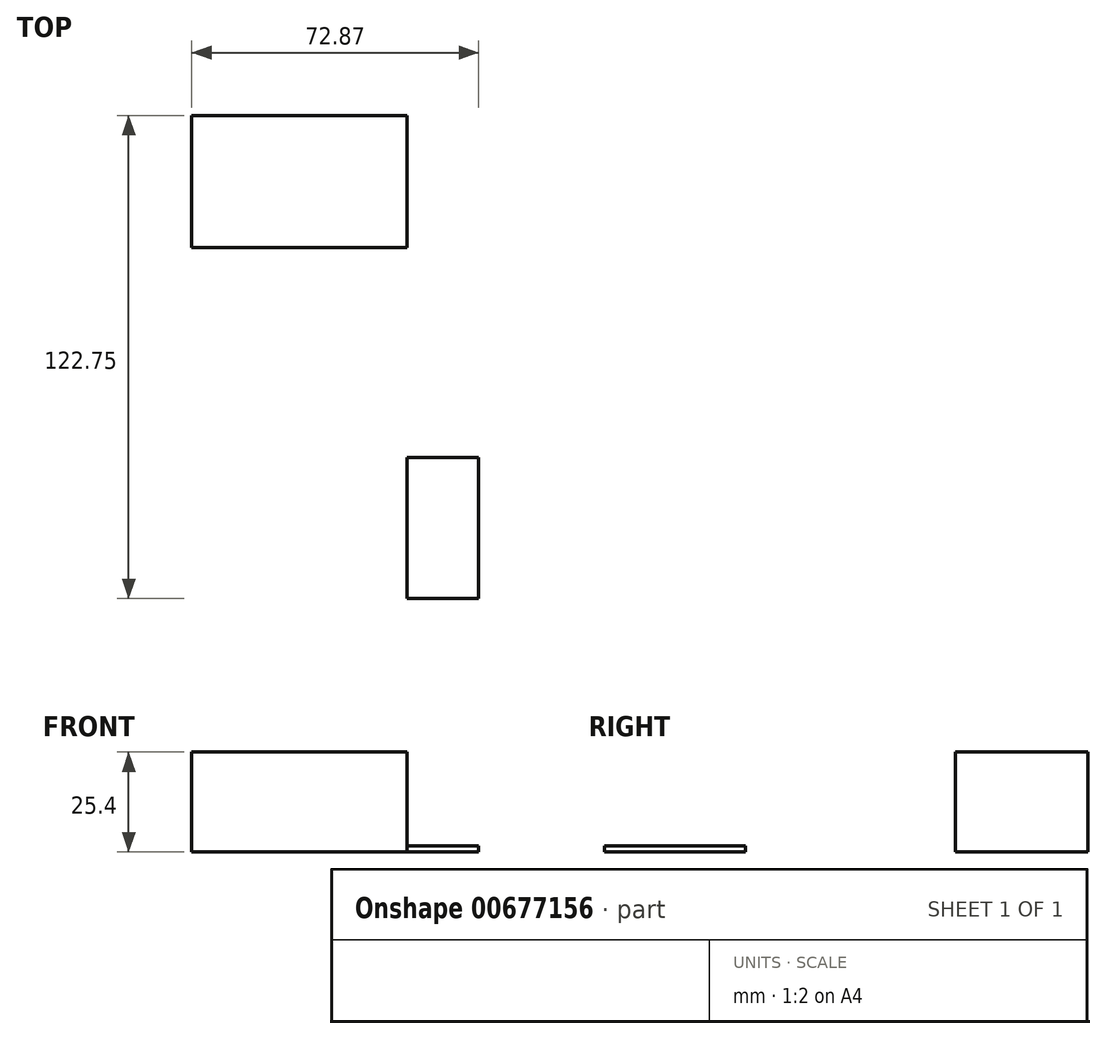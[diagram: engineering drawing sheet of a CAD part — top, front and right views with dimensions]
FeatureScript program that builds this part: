
annotation { "Feature Type Name" : "Feature", "Feature Type Description" : "" }
export const myFeature = defineFeature(function(context is Context, id is Id, definition is map)
    precondition{}
    {
        {
            var Q0;
            Q0=qCreatedBy(makeId("Top.planeOp"),FACE);
            var sketch = newSketch(context, id + "F0", { "sketchPlane" : qUnion([Q0])});
            skLineSegment(sketch, "E0.bottom", {"start": v(0, 0) * mm, "end": v(18.23, 0) * mm});
            skLineSegment(sketch, "E0.top", {"start": v(0, 35.8) * mm, "end": v(18.23, 35.8) * mm});
            skLineSegment(sketch, "E0.left", {"start": v(0, 0) * mm, "end": v(0, 35.8) * mm});
            skLineSegment(sketch, "E0.right", {"start": v(18.23, 0) * mm, "end": v(18.23, 35.8) * mm});
            skLineSegment(sketch, "E1.bottom", {"start": v(-15.75, 92.86) * mm, "end": v(6.33, 92.86) * mm});
            skLineSegment(sketch, "E1.top", {"start": v(-15.75, 103.82) * mm, "end": v(6.33, 103.82) * mm});
            skLineSegment(sketch, "E1.left", {"start": v(-15.75, 92.86) * mm, "end": v(-15.75, 103.82) * mm});
            skLineSegment(sketch, "E1.right", {"start": v(6.33, 92.86) * mm, "end": v(6.33, 103.82) * mm});
            skSolve(sketch);
        }
        {
            var Q0;
            Q0=makeQuery(id+"F0.imprint","IMPRINT",FACE,{"disambiguationData":[TD([[makeQuery(id+"F0.imprint","IMPRINT",EDGE,{"derivedFrom":sQuery(id+"F0.wireOp",EDGE,"E0.bottom")}),1.0]])]});
            extrude(context, id + "F1", {"entities" : qUnion([Q0]), "depth" : 1.59 * mm, "offsetDistance" : 25.4 * mm});
        }
        {
            var Q0;
            Q0=qCreatedBy(makeId("Top.planeOp"),FACE);
            var sketch = newSketch(context, id + "F2", { "sketchPlane" : qUnion([Q0])});
            skLineSegment(sketch, "E2.bottom", {"start": v(48.35, -47.76) * mm, "end": v(-64.85, -47.76) * mm});
            skLineSegment(sketch, "E2.top", {"start": v(48.35, 89.16) * mm, "end": v(-64.85, 89.16) * mm});
            skLineSegment(sketch, "E2.left", {"start": v(48.35, -47.76) * mm, "end": v(48.35, 89.16) * mm});
            skLineSegment(sketch, "E2.right", {"start": v(-64.85, -47.76) * mm, "end": v(-64.85, 89.16) * mm});
            skLineSegment(sketch, "E3.bottom", {"start": v(-54.64, 122.75) * mm, "end": v(0, 122.75) * mm});
            skLineSegment(sketch, "E3.top", {"start": v(-54.64, 55.5) * mm, "end": v(0, 55.5) * mm});
            skLineSegment(sketch, "E3.left", {"start": v(-54.64, 122.75) * mm, "end": v(-54.64, 55.5) * mm});
            skLineSegment(sketch, "E3.right", {"start": v(0, 122.75) * mm, "end": v(0, 55.5) * mm});
            skSolve(sketch);
        }
        {
            var Q0;
            {var subQ5=sQuery(id+"F2.wireOp",EDGE,"E3.bottom");Q0=makeQuery(id+"F2.imprint","IMPRINT",FACE,{"disambiguationData":[TD([[makeQuery(id+"F2.imprint","IMPRINT",EDGE,{"derivedFrom":subQ5}),-1.0]])]});}
            extrude(context, id + "F3", {"entities" : qUnion([Q0]), "depth" : 25.4 * mm, "offsetDistance" : 25.4 * mm});
        }
    });
